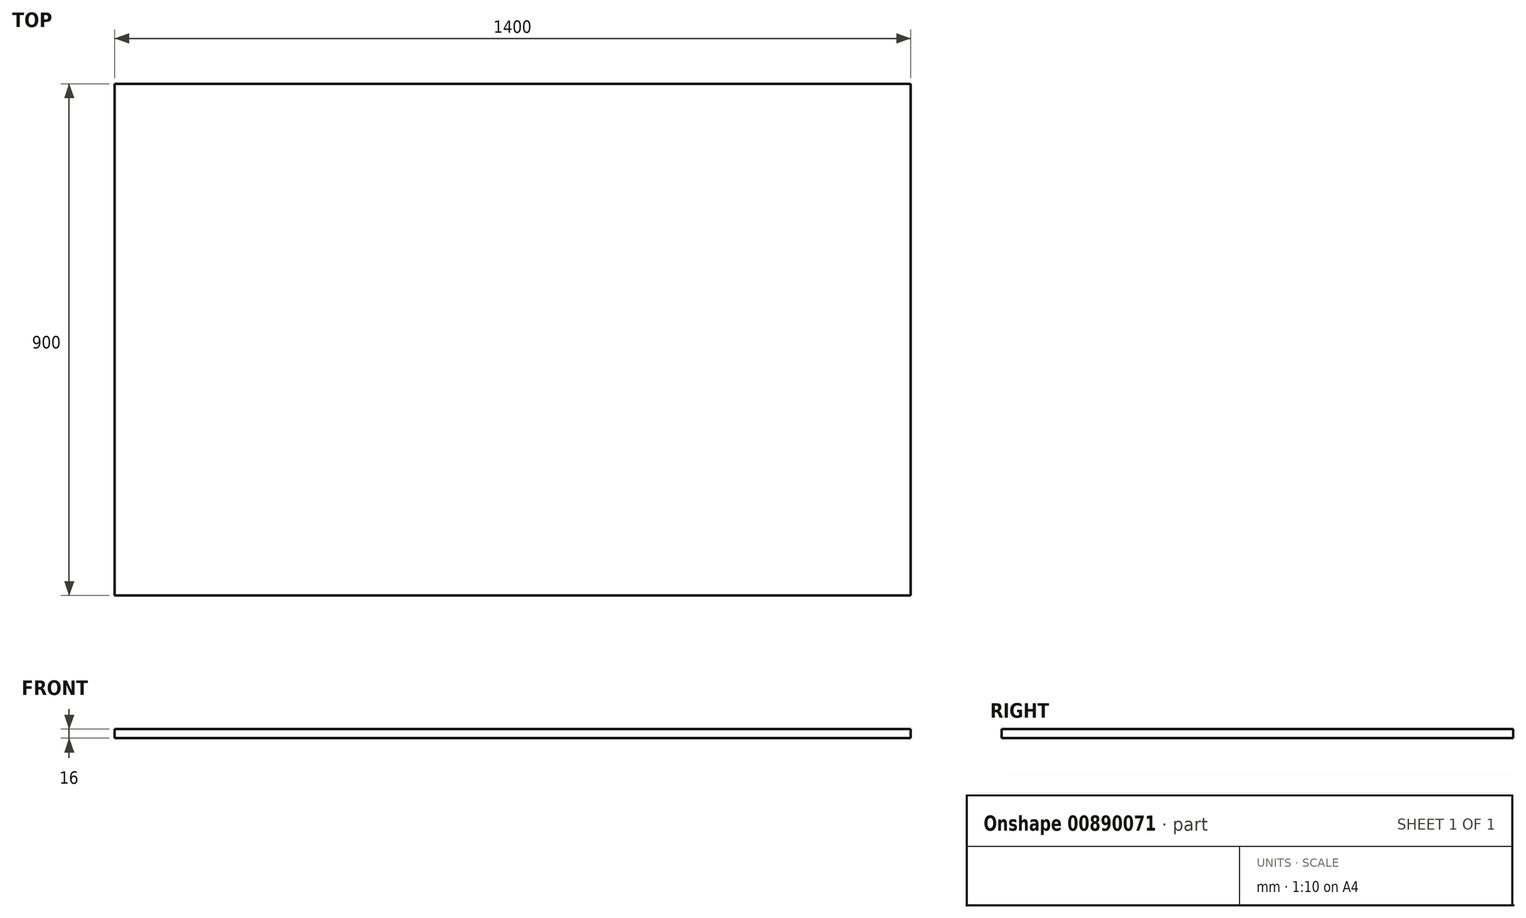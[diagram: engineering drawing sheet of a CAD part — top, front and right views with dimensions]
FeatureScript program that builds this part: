
annotation { "Feature Type Name" : "Feature", "Feature Type Description" : "" }
export const myFeature = defineFeature(function(context is Context, id is Id, definition is map)
    precondition{}
    {
        {
            var Q0;
            Q0=qCreatedBy(makeId("Top.planeOp"),FACE);
            var sketch = newSketch(context, id + "F0", { "sketchPlane" : qUnion([Q0])});
            skLineSegment(sketch, "E0.bottom", {"start": v(-700, -450) * mm, "end": v(700, -450) * mm});
            skLineSegment(sketch, "E0.top", {"start": v(-700, 450) * mm, "end": v(700, 450) * mm});
            skLineSegment(sketch, "E0.left", {"start": v(-700, -450) * mm, "end": v(-700, 450) * mm});
            skLineSegment(sketch, "E0.right", {"start": v(700, -450) * mm, "end": v(700, 450) * mm});
            skPoint(sketch, "E0.middle", {"position": v(0, 0) * mm});
            skSolve(sketch);
        }
        {
            var Q0;
            Q0=makeQuery(id+"F0.imprint","IMPRINT",FACE,{"disambiguationData":[TD([[makeQuery(id+"F0.imprint","IMPRINT",EDGE,{"derivedFrom":sQuery(id+"F0.wireOp",EDGE,"E0.bottom")}),1.0]])]});
            extrude(context, id + "F1", {"entities" : qUnion([Q0]), "depth" : 16 * mm, "offsetDistance" : 25.4 * mm});
        }
        {
            var Q0;
            Q0=makeQuery(id+"F1.opExtrude","SWEPT_FACE",FACE,{"disambiguationData":[OSD([sQuery(id+"F0.wireOp",EDGE,"E0.left")])]});
            cPlane(context, id + "F2", {"entities" : qUnion([Q0]), "cplaneType" : CPlaneType.OFFSET, "offset" : 50 * mm, "oppositeDirection" : true, "width" : 150 * mm, "height" : 150 * mm});
        }
        {
            var Q0;
            Q0=qCreatedBy(id+"F2.planeOp",FACE);
            var sketch = newSketch(context, id + "F3", { "sketchPlane" : qUnion([Q0])});
            skLineSegment(sketch, "E1", {"start": v(450, 28.5) * mm, "end": v(-450, 28.5) * mm});
            skLineSegment(sketch, "E2", {"start": v(0, 28.5) * mm, "end": v(0, -137.82) * mm, "construction": true});
            skSolve(sketch);
        }
    });
